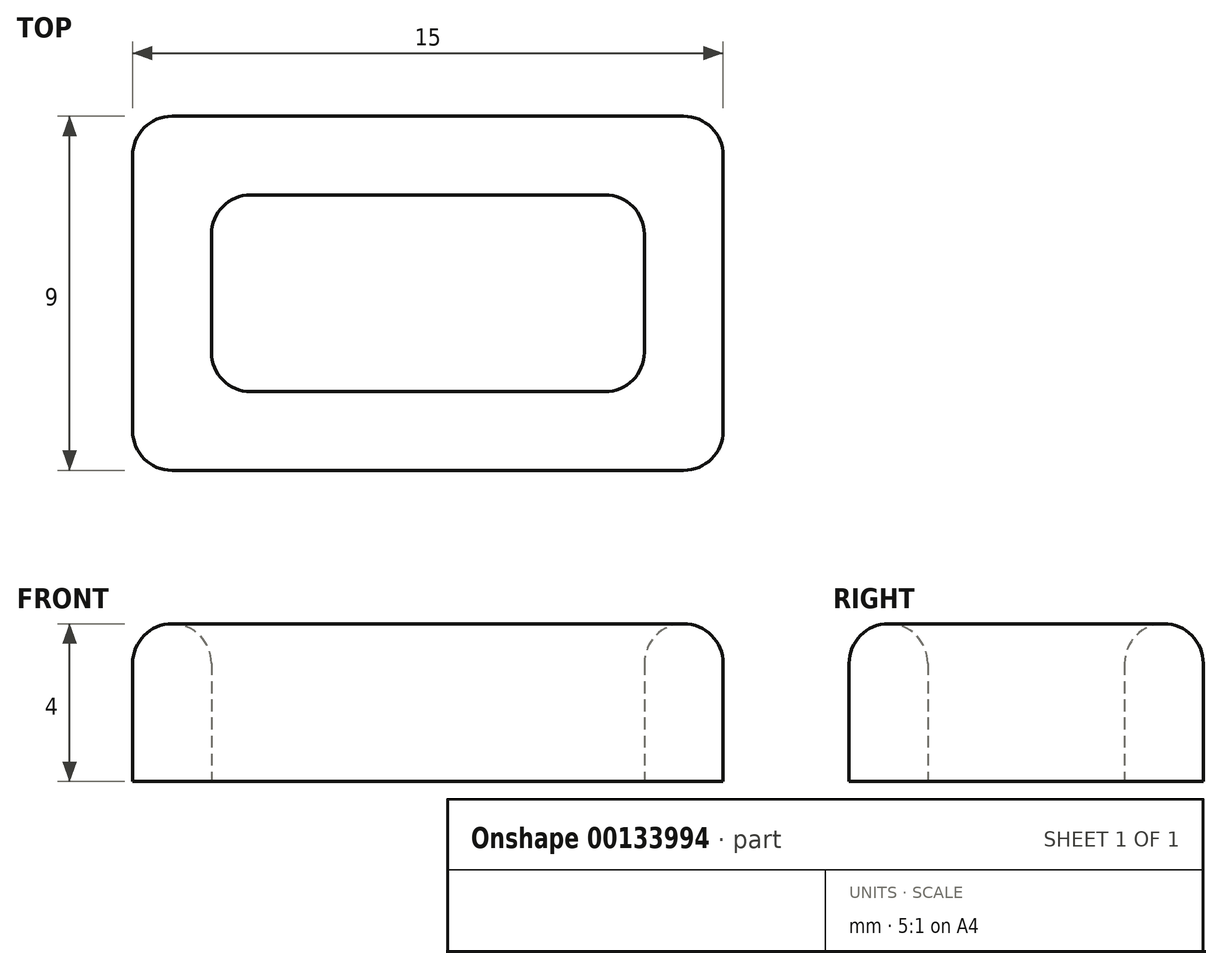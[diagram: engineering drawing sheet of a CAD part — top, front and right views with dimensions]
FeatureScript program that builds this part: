
annotation { "Feature Type Name" : "Feature", "Feature Type Description" : "" }
export const myFeature = defineFeature(function(context is Context, id is Id, definition is map)
    precondition{}
    {
        {
            var Q0;
            Q0=qCreatedBy(makeId("Top.planeOp"),FACE);
            var sketch = newSketch(context, id + "F0", { "sketchPlane" : qUnion([Q0])});
            skLineSegment(sketch, "E0.bottom", {"start": v(0, 0) * mm, "end": v(11, 0) * mm});
            skLineSegment(sketch, "E0.top", {"start": v(0, 5) * mm, "end": v(11, 5) * mm});
            skLineSegment(sketch, "E0.left", {"start": v(0, 0) * mm, "end": v(0, 5) * mm});
            skLineSegment(sketch, "E0.right", {"start": v(11, 0) * mm, "end": v(11, 5) * mm});
            skLineSegment(sketch, "E1.0", {"start": v(13, -2) * mm, "end": v(13, 7) * mm});
            skLineSegment(sketch, "E1.1", {"start": v(-2, -2) * mm, "end": v(13, -2) * mm});
            skLineSegment(sketch, "E1.2", {"start": v(-2, -2) * mm, "end": v(-2, 7) * mm});
            skLineSegment(sketch, "E1.3", {"start": v(-2, 7) * mm, "end": v(13, 7) * mm});
            skSolve(sketch);
        }
        {
            var Q0;
            Q0=makeQuery(id+"F0.imprint","IMPRINT",FACE,{"disambiguationData":[TD([[makeQuery(id+"F0.imprint","IMPRINT",EDGE,{"derivedFrom":sQuery(id+"F0.wireOp",EDGE,"E0.bottom")}),-1.0]])]});
            extrude(context, id + "F1", {"entities" : qUnion([Q0]), "depth" : 4 * mm});
        }
        {
            var Q0;
            Q0=makeQuery(id+"F1.opExtrude","CAP_EDGE",EDGE,{"disambiguationData":[OSD([sQuery(id+"F0.wireOp",EDGE,"E1.1")])],"isStart":false});
            var Q1;
            Q1=makeQuery(id+"F1.opExtrude","CAP_EDGE",EDGE,{"disambiguationData":[OSD([sQuery(id+"F0.wireOp",EDGE,"E1.0")])],"isStart":false});
            var Q2;
            Q2=makeQuery(id+"F1.opExtrude","CAP_EDGE",EDGE,{"disambiguationData":[OSD([sQuery(id+"F0.wireOp",EDGE,"E0.bottom")])],"isStart":false});
            var Q3;
            Q3=makeQuery(id+"F1.opExtrude","CAP_EDGE",EDGE,{"disambiguationData":[OSD([sQuery(id+"F0.wireOp",EDGE,"E1.2")])],"isStart":false});
            var Q4;
            Q4=makeQuery(id+"F1.opExtrude","CAP_EDGE",EDGE,{"disambiguationData":[OSD([sQuery(id+"F0.wireOp",EDGE,"E0.left")])],"isStart":false});
            var Q5;
            Q5=makeQuery(id+"F1.opExtrude","CAP_EDGE",EDGE,{"disambiguationData":[OSD([sQuery(id+"F0.wireOp",EDGE,"E1.3")])],"isStart":false});
            var Q6;
            Q6=makeQuery(id+"F1.opExtrude","CAP_EDGE",EDGE,{"disambiguationData":[OSD([sQuery(id+"F0.wireOp",EDGE,"E0.top")])],"isStart":false});
            var Q7;
            Q7=makeQuery(id+"F1.opExtrude","CAP_EDGE",EDGE,{"disambiguationData":[OSD([sQuery(id+"F0.wireOp",EDGE,"E0.right")])],"isStart":false});
            var Q8;
            Q8=makeQuery(id+"F1.opExtrude","SWEPT_EDGE",EDGE,{"disambiguationData":[OSD([sQuery(id+"F0.wireOp",EDGE,"E1.1"),sQuery(id+"F0.wireOp",EDGE,"E1.2")])]});
            var Q9;
            Q9=makeQuery(id+"F1.opExtrude","SWEPT_EDGE",EDGE,{"disambiguationData":[OSD([sQuery(id+"F0.wireOp",EDGE,"E1.0"),sQuery(id+"F0.wireOp",EDGE,"E1.1")])]});
            var Q10;
            Q10=makeQuery(id+"F1.opExtrude","SWEPT_EDGE",EDGE,{"disambiguationData":[OSD([sQuery(id+"F0.wireOp",EDGE,"E0.bottom"),sQuery(id+"F0.wireOp",EDGE,"E0.right")])]});
            var Q11;
            Q11=makeQuery(id+"F1.opExtrude","SWEPT_EDGE",EDGE,{"disambiguationData":[OSD([sQuery(id+"F0.wireOp",EDGE,"E0.bottom"),sQuery(id+"F0.wireOp",EDGE,"E0.left")])]});
            var Q12;
            Q12=makeQuery(id+"F1.opExtrude","SWEPT_EDGE",EDGE,{"disambiguationData":[OSD([sQuery(id+"F0.wireOp",EDGE,"E1.2"),sQuery(id+"F0.wireOp",EDGE,"E1.3")])]});
            var Q13;
            Q13=makeQuery(id+"F1.opExtrude","SWEPT_EDGE",EDGE,{"disambiguationData":[OSD([sQuery(id+"F0.wireOp",EDGE,"E1.0"),sQuery(id+"F0.wireOp",EDGE,"E1.3")])]});
            var Q14;
            Q14=makeQuery(id+"F1.opExtrude","SWEPT_EDGE",EDGE,{"disambiguationData":[OSD([sQuery(id+"F0.wireOp",EDGE,"E0.top"),sQuery(id+"F0.wireOp",EDGE,"E0.right")])]});
            var Q15;
            Q15=makeQuery(id+"F1.opExtrude","SWEPT_EDGE",EDGE,{"disambiguationData":[OSD([sQuery(id+"F0.wireOp",EDGE,"E0.top"),sQuery(id+"F0.wireOp",EDGE,"E0.left")])]});
            fillet(context, id + "F2", {"entities" : qUnion([Q0, Q1, Q2, Q3, Q4, Q5, Q6, Q7, Q8, Q9, Q10, Q11, Q12, Q13, Q14, Q15]), "radius" : 1 * mm, "tangentPropagation" : true, "allowEdgeOverflow" : false});
        }
    });
